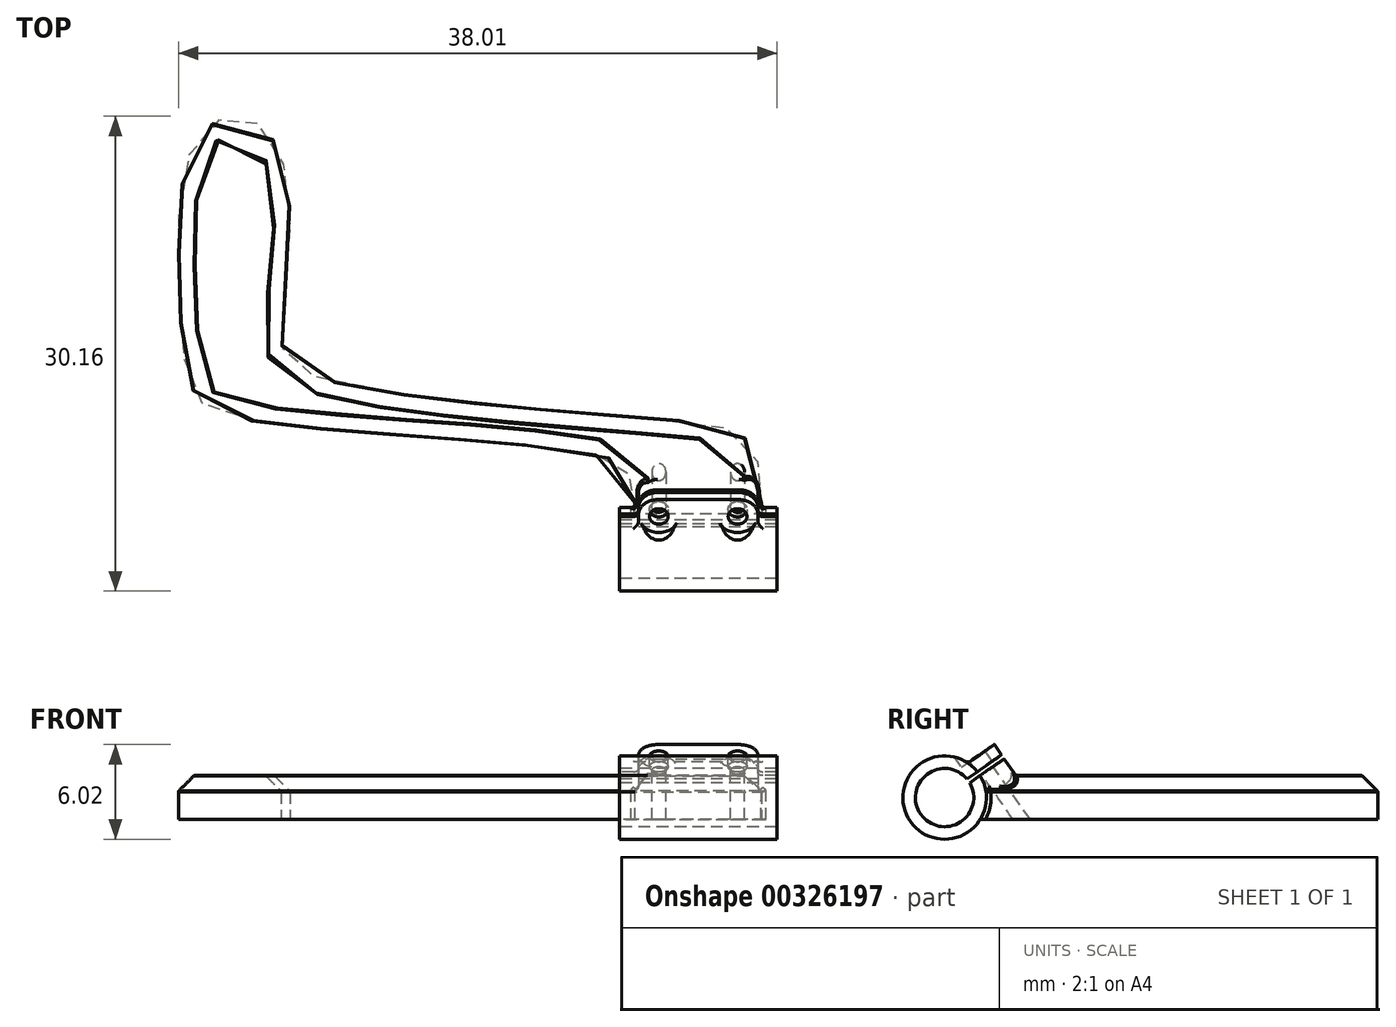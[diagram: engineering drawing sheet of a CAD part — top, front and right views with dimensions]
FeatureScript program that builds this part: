
annotation { "Feature Type Name" : "Feature", "Feature Type Description" : "" }
export const myFeature = defineFeature(function(context is Context, id is Id, definition is map)
    precondition{}
    {
        {
            var Q0;
            Q0=qCreatedBy(makeId("Top.planeOp"),FACE);
            var sketch = newSketch(context, id + "F0", { "sketchPlane" : qUnion([Q0])});
            skLineSegment(sketch, "E0", {"start": v(0, 0) * mm, "end": v(8, 0) * mm});
            skLineSegment(sketch, "E1", {"start": v(8, 0) * mm, "end": v(8, 0.6) * mm});
            skLineSegment(sketch, "E2", {"start": v(8, 0.6) * mm, "end": v(0, 0.6) * mm});
            skLineSegment(sketch, "E3", {"start": v(0, 0.6) * mm, "end": v(0, 0) * mm});
            skFitSpline(sketch, "E4", {"points": [v(0, 0.6) * mm, v(-0.36, 2.8) * mm, v(-2.22, 4.02) * mm, v(-24.68, 6.3) * mm, v(-28.15, 8.37) * mm, v(-29, 16.04) * mm, v(-28.1, 23.61) * mm, v(-25.63, 25.6) * mm, v(-23.1, 24.28) * mm, v(-21.95, 17.87) * mm, v(-22.45, 11.26) * mm, v(-20.46, 9.12) * mm, v(1.88, 6.35) * mm, v(7.53, 4.39) * mm, v(8, 0.6) * mm], "startDerivative": vector(0, 68.07) * mm, "endDerivative": vector(0, -27.38) * mm});
            skPoint(sketch, "E5", {"position": v(8, 0.3) * mm});
            skSolve(sketch);
        }
        {
            var Q0;
            Q0=qSketchRegion(id+"F0",true);
            extrude(context, id + "F1", {"entities" : qUnion([Q0]), "depth" : 2.8 * mm});
        }
        {
            var Q0;
            Q0=makeQuery(id+"F1.opExtrude","CAP_EDGE",EDGE,{"disambiguationData":[OSD([sQuery(id+"F0.wireOp",EDGE,"E4")])],"isStart":false});
            chamfer(context, id + "F2", {"entities" : qUnion([Q0]), "chamferType" : ChamferType.TWO_OFFSETS, "width1" : 1 * mm, "oppositeDirection" : false, "width2" : 1 * mm, "tangentPropagation" : true});
        }
        {
            var Q0;
            Q0=qCreatedBy(makeId("Right.planeOp"),FACE);
            var sketch = newSketch(context, id + "F3", { "sketchPlane" : qUnion([Q0])});
            skCircle(sketch, "E6.converted", {"center": v(-1.9, 1.4) * mm, "radius": 2.65 * mm});
            skCircle(sketch, "E7.converted", {"center": v(-1.9, 1.4) * mm, "radius": 1.85 * mm});
            skLineSegment(sketch, "E8", {"start": v(-1.9, 1.4) * mm, "end": v(0, 1.4) * mm, "construction": true});
            skSolve(sketch);
        }
        {
            var Q0;
            Q0=makeQuery(id+"F3.imprint","IMPRINT",FACE,{"disambiguationData":[TD([[makeQuery(id+"F3.imprint","IMPRINT",EDGE,{"derivedFrom":sQuery(id+"F3.wireOp",EDGE,"E6.converted")}),1.0]])]});
            extrude(context, id + "F4", {"entities" : qUnion([Q0]), "operationType" : NewBodyOperationType.ADD, "depth" : 9 * mm, "hasSecondDirection" : true, "secondDirectionOppositeDirection" : true, "secondDirectionDepth" : 1 * mm});
        }
        {
            var Q0;
            Q0=makeQuery(id+"F4.opExtrude","CAP_FACE",FACE,{"disambiguationData":[OSD([sQuery(id+"F3.wireOp",EDGE,"E6.converted"),sQuery(id+"F3.wireOp",EDGE,"E7.converted")])],"isStart":true});
            cPlane(context, id + "F5", {"entities" : qUnion([Q0]), "cplaneType" : CPlaneType.OFFSET, "offset" : 5 * mm, "oppositeDirection" : true, "width" : 150 * mm, "height" : 150 * mm});
        }
        {
            var Q0;
            Q0=qCreatedBy(id+"F5.planeOp",FACE);
            var sketch = newSketch(context, id + "F6", { "sketchPlane" : qUnion([Q0])});
            skLineSegment(sketch, "E9", {"start": v(1.9, 1.4) * mm, "end": v(0.51, 2.37) * mm, "construction": true});
            skLineSegment(sketch, "E10.0", {"start": v(2.16, 1.4) * mm, "end": v(0.16, 2.8) * mm});
            skLineSegment(sketch, "E11.0", {"start": v(1.64, 1.4) * mm, "end": v(-0.36, 2.8) * mm});
            skLineSegment(sketch, "E12", {"start": v(-0.36, 2.8) * mm, "end": v(0.16, 2.8) * mm});
            skLineSegment(sketch, "E13", {"start": v(2.16, 1.4) * mm, "end": v(1.64, 1.4) * mm});
            skLineSegment(sketch, "E14", {"start": v(0.16, 2.8) * mm, "end": v(-1.71, 4.11) * mm});
            skLineSegment(sketch, "E15", {"start": v(-1.71, 4.11) * mm, "end": v(-1.25, 4.77) * mm});
            skLineSegment(sketch, "E16", {"start": v(-1.25, 4.77) * mm, "end": v(1.56, 2.8) * mm});
            skLineSegment(sketch, "E17", {"start": v(1.56, 2.8) * mm, "end": v(1.1, 2.14) * mm});
            skLineSegment(sketch, "E18", {"start": v(-0.36, 2.8) * mm, "end": v(-1.88, 3.87) * mm});
            skLineSegment(sketch, "E19", {"start": v(-1.88, 3.87) * mm, "end": v(-2.63, 2.8) * mm});
            skLineSegment(sketch, "E20", {"start": v(-2.63, 2.8) * mm, "end": v(-0.36, 2.8) * mm});
            skCircle(sketch, "E21.0", {"center": v(1.9, 1.4) * mm, "radius": 1.85 * mm, "construction": true});
            skPoint(sketch, "E22", {"position": v(0.55, 3.5) * mm});
            skLineSegment(sketch, "E23", {"start": v(-2.63, 2.8) * mm, "end": v(-2.63, 1.7) * mm});
            skLineSegment(sketch, "E24", {"start": v(-2.63, 1.7) * mm, "end": v(0.79, 1.7) * mm});
            skLineSegment(sketch, "E25", {"start": v(0.79, 1.7) * mm, "end": v(0.93, 1.9) * mm});
            skCircle(sketch, "E26", {"center": v(1.9, 1.4) * mm, "radius": 2.5 * mm, "construction": true});
            skLineSegment(sketch, "E27", {"start": v(-1.71, 4.11) * mm, "end": v(-1.88, 3.87) * mm});
            skCircle(sketch, "E28", {"center": v(1.9, 1.4) * mm, "radius": 1.85 * mm});
            skLineSegment(sketch, "E29", {"start": v(-2.63, 2.8) * mm, "end": v(-2.88, 2.44) * mm});
            skLineSegment(sketch, "E30", {"start": v(-2.88, 2.44) * mm, "end": v(-2.88, 1.7) * mm});
            skLineSegment(sketch, "E31", {"start": v(-2.88, 1.7) * mm, "end": v(-2.63, 1.7) * mm});
            skSolve(sketch);
        }
        {
            var Q0;
            {var subQ0=sQuery(id+"F6.wireOp",EDGE,"E14");Q0=makeQuery(id+"F6.imprint","IMPRINT",FACE,{"disambiguationData":[TD([[makeQuery(id+"F6.imprint","IMPRINT",EDGE,{"derivedFrom":subQ0}),-1.0]])]});}
            var Q1;
            Q1=makeQuery(id+"F6.imprint","IMPRINT",FACE,{"disambiguationData":[TD([[makeQuery(id+"F6.imprint","IMPRINT",EDGE,{"derivedFrom":sQuery(id+"F6.wireOp",EDGE,"E18")}),1.0]])]});
            var Q2;
            {var subQ0=sQuery(id+"F6.wireOp",EDGE,"E20");Q2=makeQuery(id+"F6.imprint","IMPRINT",FACE,{"disambiguationData":[TD([[makeQuery(id+"F6.imprint","IMPRINT",EDGE,{"derivedFrom":subQ0}),-1.0]])]});}
            var Q3;
            Q3=makeQuery(id+"F6.imprint","IMPRINT",FACE,{"disambiguationData":[TD([[makeQuery(id+"F6.imprint","IMPRINT",EDGE,{"derivedFrom":sQuery(id+"F6.wireOp",EDGE,"E23")}),-1.0]])]});
            extrude(context, id + "F7", {"entities" : qUnion([Q0, Q1, Q2, Q3]), "operationType" : NewBodyOperationType.ADD, "depth" : 3.8 * mm, "hasSecondDirection" : true, "secondDirectionOppositeDirection" : true, "secondDirectionDepth" : 3.8 * mm});
        }
        {
            var Q0;
            {var subQ0=sQuery(id+"F6.wireOp",EDGE,"E12");Q0=makeQuery(id+"F6.imprint","IMPRINT",FACE,{"disambiguationData":[TD([[makeQuery(id+"F6.imprint","IMPRINT",EDGE,{"derivedFrom":subQ0}),-1.0]])]});}
            var Q1;
            Q1=makeQuery(id+"F6.imprint","IMPRINT",FACE,{"disambiguationData":[TD([[makeQuery(id+"F6.imprint","IMPRINT",EDGE,{"derivedFrom":sQuery(id+"F6.wireOp",EDGE,"E12")}),1.0]])]});
            var Q2;
            {var subQ1=sQuery(id+"F6.wireOp",EDGE,"E18");Q2=makeQuery(id+"F6.imprint","IMPRINT",FACE,{"disambiguationData":[TD([[makeQuery(id+"F6.imprint","IMPRINT",EDGE,{"derivedFrom":subQ1}),-1.0]])]});}
            extrude(context, id + "F8", {"entities" : qUnion([Q0, Q1, Q2]), "operationType" : NewBodyOperationType.REMOVE, "endBound" : BoundingType.THROUGH_ALL, "oppositeDirection" : true, "depth" : 25 * mm, "hasSecondDirection" : true, "secondDirectionBound" : BoundingType.THROUGH_ALL, "secondDirectionOppositeDirection" : false, "secondDirectionDepth" : 25 * mm});
        }
        {
            var Q0;
            Q0=makeQuery(id+"F7.opExtrude","SWEPT_FACE",FACE,{"disambiguationData":[OSD([sQuery(id+"F6.wireOp",EDGE,"E16")])]});
            var sketch = newSketch(context, id + "F9", { "sketchPlane" : qUnion([Q0])});
            skCircle(sketch, "E32", {"center": v(1.5, 2.46) * mm, "radius": 0.6 * mm});
            skCircle(sketch, "E33", {"center": v(6.5, 2.46) * mm, "radius": 0.6 * mm});
            skCircle(sketch, "E34", {"center": v(6.5, 2.46) * mm, "radius": 0.44 * mm});
            skCircle(sketch, "E35", {"center": v(1.5, 2.46) * mm, "radius": 0.44 * mm});
            skCircle(sketch, "E36", {"center": v(1.5, 2.46) * mm, "radius": 1.25 * mm});
            skCircle(sketch, "E37", {"center": v(6.5, 2.46) * mm, "radius": 1.25 * mm});
            skSolve(sketch);
        }
        {
            var Q0;
            Q0=makeQuery(id+"F9.imprint","IMPRINT",FACE,{"disambiguationData":[TD([[makeQuery(id+"F9.imprint","IMPRINT",EDGE,{"derivedFrom":sQuery(id+"F9.wireOp",EDGE,"E35")}),1.0]])]});
            var Q1;
            Q1=makeQuery(id+"F9.imprint","IMPRINT",FACE,{"disambiguationData":[TD([[makeQuery(id+"F9.imprint","IMPRINT",EDGE,{"derivedFrom":sQuery(id+"F9.wireOp",EDGE,"E34")}),1.0]])]});
            extrude(context, id + "F10", {"entities" : qUnion([Q0, Q1]), "operationType" : NewBodyOperationType.REMOVE, "endBound" : BoundingType.THROUGH_ALL, "oppositeDirection" : true, "depth" : 25 * mm});
        }
        {
            var Q0;
            Q0=makeQuery(id+"F9.imprint","IMPRINT",FACE,{"disambiguationData":[TD([[makeQuery(id+"F9.imprint","IMPRINT",EDGE,{"derivedFrom":sQuery(id+"F9.wireOp",EDGE,"E35")}),-1.0]])]});
            var Q1;
            Q1=makeQuery(id+"F9.imprint","IMPRINT",FACE,{"disambiguationData":[TD([[makeQuery(id+"F9.imprint","IMPRINT",EDGE,{"derivedFrom":sQuery(id+"F9.wireOp",EDGE,"E34")}),-1.0]])]});
            var Q2;
            {var subQ0=sQuery(id+"F9.wireOp",EDGE,"E32");var subQ1=makeQuery(id+"F7.boolean.opBoolean","INTERSECT",EDGE,{"derivedFrom":[makeQuery(id+"F4.opExtrude","SWEPT_FACE",FACE,{"disambiguationData":[OSD([sQuery(id+"F3.wireOp",EDGE,"E6.converted")])]}),makeQuery(id+"F7.opExtrude","SWEPT_FACE",FACE,{"disambiguationData":[OSD([sQuery(id+"F6.wireOp",EDGE,"E16")])]})]});var subQ2=makeQuery(id+"F9.imprint","INTERSECT",VERTEX,{"disambiguationData":[OD(0.0)],"derivedFrom":[subQ1,subQ0]});Q2=makeQuery(id+"F9.imprint","IMPRINT",FACE,{"disambiguationData":[TD([[makeQuery(id+"F9.imprint","IMPRINT",EDGE,{"disambiguationData":[TD([[subQ2,-1.0]])],"derivedFrom":subQ0}),1.0]])]});}
            var Q3;
            {var subQ0=sQuery(id+"F9.wireOp",EDGE,"E33");var subQ1=makeQuery(id+"F7.boolean.opBoolean","INTERSECT",EDGE,{"derivedFrom":[makeQuery(id+"F4.opExtrude","SWEPT_FACE",FACE,{"disambiguationData":[OSD([sQuery(id+"F3.wireOp",EDGE,"E6.converted")])]}),makeQuery(id+"F7.opExtrude","SWEPT_FACE",FACE,{"disambiguationData":[OSD([sQuery(id+"F6.wireOp",EDGE,"E16")])]})]});var subQ2=makeQuery(id+"F9.imprint","INTERSECT",VERTEX,{"disambiguationData":[OD(0.0)],"derivedFrom":[subQ1,subQ0]});Q3=makeQuery(id+"F9.imprint","IMPRINT",FACE,{"disambiguationData":[TD([[makeQuery(id+"F9.imprint","IMPRINT",EDGE,{"disambiguationData":[TD([[subQ2,1.0]])],"derivedFrom":subQ0}),1.0]])]});}
            extrude(context, id + "F11", {"entities" : qUnion([Q0, Q1, Q2, Q3]), "operationType" : NewBodyOperationType.REMOVE, "endBound" : BoundingType.UP_TO_NEXT, "oppositeDirection" : true, "depth" : 25 * mm, "hasSecondDirection" : true, "secondDirectionOppositeDirection" : false, "secondDirectionDepth" : 25 * mm});
        }
        {
            var Q0;
            {var subQ0=sQuery(id+"F9.wireOp",EDGE,"E36");var subQ1=makeQuery(id+"F7.boolean.opBoolean","INTERSECT",EDGE,{"derivedFrom":[makeQuery(id+"F4.opExtrude","SWEPT_FACE",FACE,{"disambiguationData":[OSD([sQuery(id+"F3.wireOp",EDGE,"E6.converted")])]}),makeQuery(id+"F7.opExtrude","SWEPT_FACE",FACE,{"disambiguationData":[OSD([sQuery(id+"F6.wireOp",EDGE,"E16")])]})]});var subQ2=makeQuery(id+"F9.imprint","INTERSECT",VERTEX,{"disambiguationData":[OD(0.0)],"derivedFrom":[subQ1,subQ0]});Q0=makeQuery(id+"F9.imprint","IMPRINT",FACE,{"disambiguationData":[TD([[makeQuery(id+"F9.imprint","IMPRINT",EDGE,{"disambiguationData":[TD([[subQ2,-1.0]])],"derivedFrom":subQ0}),1.0]])]});}
            var Q1;
            {var subQ0=sQuery(id+"F9.wireOp",EDGE,"E37");var subQ1=makeQuery(id+"F7.boolean.opBoolean","INTERSECT",EDGE,{"derivedFrom":[makeQuery(id+"F4.opExtrude","SWEPT_FACE",FACE,{"disambiguationData":[OSD([sQuery(id+"F3.wireOp",EDGE,"E6.converted")])]}),makeQuery(id+"F7.opExtrude","SWEPT_FACE",FACE,{"disambiguationData":[OSD([sQuery(id+"F6.wireOp",EDGE,"E16")])]})]});var subQ2=makeQuery(id+"F9.imprint","INTERSECT",VERTEX,{"disambiguationData":[OD(0.0)],"derivedFrom":[subQ1,subQ0]});Q1=makeQuery(id+"F9.imprint","IMPRINT",FACE,{"disambiguationData":[TD([[makeQuery(id+"F9.imprint","IMPRINT",EDGE,{"disambiguationData":[TD([[subQ2,1.0]])],"derivedFrom":subQ0}),1.0]])]});}
            extrude(context, id + "F12", {"entities" : qUnion([Q0, Q1]), "operationType" : NewBodyOperationType.REMOVE, "endBound" : BoundingType.UP_TO_NEXT, "depth" : 25 * mm});
        }
        {
            var Q0;
            Q0=makeQuery(id+"F7.opExtrude","CAP_EDGE",EDGE,{"disambiguationData":[OSD([sQuery(id+"F6.wireOp",EDGE,"E19")])],"isStart":false});
            var Q1;
            Q1=makeQuery(id+"F7.opExtrude","CAP_EDGE",EDGE,{"disambiguationData":[OSD([sQuery(id+"F6.wireOp",EDGE,"E15")])],"isStart":false});
            var Q2;
            Q2=makeQuery(id+"F7.opExtrude","CAP_EDGE",EDGE,{"disambiguationData":[OSD([sQuery(id+"F6.wireOp",EDGE,"E19")])],"isStart":true});
            var Q3;
            Q3=makeQuery(id+"F7.opExtrude","CAP_EDGE",EDGE,{"disambiguationData":[OSD([sQuery(id+"F6.wireOp",EDGE,"E15")])],"isStart":true});
            fillet(context, id + "F13", {"entities" : qUnion([Q0, Q1, Q2, Q3]), "radius" : 1.2 * mm, "tangentPropagation" : true, "allowEdgeOverflow" : false});
        }
        {
            var Q0;
            Q0=makeQuery(id+"F7.boolean.opBoolean","INTERSECT",EDGE,{"derivedFrom":[makeQuery(id+"F2.opChamfer","BLEND_FACE",FACE,{"disambiguationData":[OSD([sQuery(id+"F0.wireOp",EDGE,"E4")])]}),makeQuery(id+"F7.opExtrude","CAP_FACE",FACE,{"disambiguationData":[OSD([sQuery(id+"F6.wireOp",EDGE,"E11.0"),sQuery(id+"F6.wireOp",EDGE,"E18"),sQuery(id+"F6.wireOp",EDGE,"E19"),sQuery(id+"F6.wireOp",EDGE,"E23"),sQuery(id+"F6.wireOp",EDGE,"E24"),sQuery(id+"F6.wireOp",EDGE,"E28")])],"isStart":true})]});
            var Q1;
            Q1=makeQuery(id+"F13.opFillet","BLEND_EDGE",EDGE,{"blendedFrom":[makeQuery(id+"F7.opExtrude","CAP_EDGE",EDGE,{"disambiguationData":[OSD([sQuery(id+"F6.wireOp",EDGE,"E19")])],"isStart":false}),makeQuery(id+"F2.opChamfer","BLEND_FACE",FACE,{"disambiguationData":[OSD([sQuery(id+"F0.wireOp",EDGE,"E4")])]})],"blendedInto":[makeQuery(id+"F2.opChamfer","BLEND_FACE",FACE,{"disambiguationData":[OSD([sQuery(id+"F0.wireOp",EDGE,"E4")])]})]});
            var Q2;
            {var subQ0=sQuery(id+"F9.wireOp",EDGE,"E36");var subQ1=sQuery(id+"F6.wireOp",EDGE,"E16");var subQ2=sQuery(id+"F3.wireOp",EDGE,"E6.converted");var subQ3=makeQuery(id+"F7.opExtrude","SWEPT_FACE",FACE,{"disambiguationData":[OSD([subQ1])]});var subQ4=makeQuery(id+"F4.opExtrude","SWEPT_FACE",FACE,{"disambiguationData":[OSD([subQ2])]});var subQ5=sQuery(id+"F9.wireOp",EDGE,"E37");Q2=makeQuery(id+"F12.boolean.opBoolean","SPLIT",EDGE,{"disambiguationData":[TD([subQ4,subQ3,makeQuery(id+"F12.opExtrude","SWEPT_FACE",FACE,{"disambiguationData":[OSD([subQ0])]}),makeQuery(id+"F12.opExtrude","CAP_FACE",FACE,{"disambiguationData":[OSD([subQ2,subQ1,subQ0])],"isStart":true}),makeQuery(id+"F12.opExtrude","SWEPT_FACE",FACE,{"disambiguationData":[OSD([subQ5])]}),makeQuery(id+"F12.opExtrude","CAP_FACE",FACE,{"disambiguationData":[OSD([subQ2,subQ1,subQ5])],"isStart":true})])],"derivedFrom":makeQuery(id+"F7.boolean.opBoolean","INTERSECT",EDGE,{"derivedFrom":[subQ4,subQ3]})});}
            var Q3;
            {var subQ0=sQuery(id+"F6.wireOp",EDGE,"E16");var subQ1=makeQuery(id+"F7.opExtrude","SWEPT_FACE",FACE,{"disambiguationData":[OSD([subQ0])]});var subQ2=sQuery(id+"F9.wireOp",EDGE,"E36");var subQ3=sQuery(id+"F3.wireOp",EDGE,"E6.converted");var subQ4=makeQuery(id+"F4.opExtrude","SWEPT_FACE",FACE,{"disambiguationData":[OSD([subQ3])]});Q3=makeQuery(id+"F12.boolean.opBoolean","SPLIT",EDGE,{"disambiguationData":[TD([subQ4,makeQuery(id+"F7.opExtrude","CAP_FACE",FACE,{"disambiguationData":[OSD([sQuery(id+"F6.wireOp",EDGE,"E14"),sQuery(id+"F6.wireOp",EDGE,"E15"),subQ0,sQuery(id+"F6.wireOp",EDGE,"E28")])],"isStart":false}),subQ1,makeQuery(id+"F12.opExtrude","SWEPT_FACE",FACE,{"disambiguationData":[OSD([subQ2])]}),makeQuery(id+"F12.opExtrude","CAP_FACE",FACE,{"disambiguationData":[OSD([subQ3,subQ0,subQ2])],"isStart":true}),makeQuery(id+"F12.opExtrude","CAP_FACE",FACE,{"disambiguationData":[OSD([subQ3,subQ0,sQuery(id+"F9.wireOp",EDGE,"E37")])],"isStart":true})])],"derivedFrom":makeQuery(id+"F7.boolean.opBoolean","INTERSECT",EDGE,{"derivedFrom":[subQ4,subQ1]})});}
            var Q4;
            Q4=makeQuery(id+"F13.opFillet","BLEND_EDGE",EDGE,{"disambiguationData":[OD(1.0)],"blendedFrom":[makeQuery(id+"F7.opExtrude","CAP_EDGE",EDGE,{"disambiguationData":[OSD([sQuery(id+"F6.wireOp",EDGE,"E19")])],"isStart":true}),makeQuery(id+"F2.opChamfer","BLEND_FACE",FACE,{"disambiguationData":[OSD([sQuery(id+"F0.wireOp",EDGE,"E4")])]})],"blendedInto":[makeQuery(id+"F2.opChamfer","BLEND_FACE",FACE,{"disambiguationData":[OSD([sQuery(id+"F0.wireOp",EDGE,"E4")])]})]});
            var Q5;
            {var subQ0=sQuery(id+"F6.wireOp",EDGE,"E16");var subQ1=sQuery(id+"F3.wireOp",EDGE,"E6.converted");var subQ2=makeQuery(id+"F7.opExtrude","SWEPT_FACE",FACE,{"disambiguationData":[OSD([subQ0])]});var subQ3=makeQuery(id+"F4.opExtrude","SWEPT_FACE",FACE,{"disambiguationData":[OSD([subQ1])]});var subQ4=sQuery(id+"F9.wireOp",EDGE,"E37");Q5=makeQuery(id+"F12.boolean.opBoolean","SPLIT",EDGE,{"disambiguationData":[TD([subQ3,makeQuery(id+"F7.opExtrude","CAP_FACE",FACE,{"disambiguationData":[OSD([sQuery(id+"F6.wireOp",EDGE,"E14"),sQuery(id+"F6.wireOp",EDGE,"E15"),subQ0,sQuery(id+"F6.wireOp",EDGE,"E28")])],"isStart":true}),subQ2,makeQuery(id+"F12.opExtrude","CAP_FACE",FACE,{"disambiguationData":[OSD([subQ1,subQ0,sQuery(id+"F9.wireOp",EDGE,"E36")])],"isStart":true}),makeQuery(id+"F12.opExtrude","SWEPT_FACE",FACE,{"disambiguationData":[OSD([subQ4])]}),makeQuery(id+"F12.opExtrude","CAP_FACE",FACE,{"disambiguationData":[OSD([subQ1,subQ0,subQ4])],"isStart":true})])],"derivedFrom":makeQuery(id+"F7.boolean.opBoolean","INTERSECT",EDGE,{"derivedFrom":[subQ3,subQ2]})});}
            var Q6;
            Q6=makeQuery(id+"F4.boolean.opBoolean","INTERSECT",EDGE,{"derivedFrom":[makeQuery(id+"F1.opExtrude","SWEPT_FACE",FACE,{"disambiguationData":[OSD([sQuery(id+"F0.wireOp",EDGE,"E3")])]}),makeQuery(id+"F4.opExtrude","SWEPT_FACE",FACE,{"disambiguationData":[OSD([sQuery(id+"F3.wireOp",EDGE,"E6.converted")])]})]});
            var Q7;
            Q7=makeQuery(id+"F4.boolean.opBoolean","INTERSECT",EDGE,{"derivedFrom":[makeQuery(id+"F1.opExtrude","SWEPT_FACE",FACE,{"disambiguationData":[OSD([sQuery(id+"F0.wireOp",EDGE,"E1")])]}),makeQuery(id+"F4.opExtrude","SWEPT_FACE",FACE,{"disambiguationData":[OSD([sQuery(id+"F3.wireOp",EDGE,"E6.converted")])]})]});
            var Q8;
            Q8=makeQuery(id+"F4.boolean.opBoolean","INTERSECT",EDGE,{"disambiguationData":[OD(0.0)],"derivedFrom":[makeQuery(id+"F1.opExtrude","SWEPT_FACE",FACE,{"disambiguationData":[OSD([sQuery(id+"F0.wireOp",EDGE,"E4")])]}),makeQuery(id+"F4.opExtrude","SWEPT_FACE",FACE,{"disambiguationData":[OSD([sQuery(id+"F3.wireOp",EDGE,"E6.converted")])]})]});
            var Q9;
            Q9=makeQuery(id+"F7.boolean.opBoolean","INTERSECT",EDGE,{"derivedFrom":[makeQuery(id+"F1.opExtrude","CAP_FACE",FACE,{"disambiguationData":[OSD([sQuery(id+"F0.wireOp",EDGE,"E0"),sQuery(id+"F0.wireOp",EDGE,"E1"),sQuery(id+"F0.wireOp",EDGE,"E3"),sQuery(id+"F0.wireOp",EDGE,"E4")])],"isStart":false}),makeQuery(id+"F7.opExtrude","SWEPT_FACE",FACE,{"disambiguationData":[OSD([sQuery(id+"F6.wireOp",EDGE,"E19"),sQuery(id+"F6.wireOp",EDGE,"E29")])]})]});
            fillet(context, id + "F14", {"entities" : qUnion([Q0, Q1, Q2, Q3, Q4, Q5, Q6, Q7, Q8, Q9]), "radius" : 0.3 * mm, "tangentPropagation" : true, "allowEdgeOverflow" : false});
        }
        {
            var Q0;
            Q0=makeQuery(id+"F7eM0luwQxw6Xwf_1.opExtrude","TWEAK_EDGE",EDGE,{"derivedFrom":[makeQuery(id+"F1.opExtrude","CAP_EDGE",EDGE,{"disambiguationData":[OSD([sQuery(id+"F0.wireOp",EDGE,"E0")])],"isStart":true}),makeQuery(id+"F4.opExtrude","SWEPT_FACE",FACE,{"disambiguationData":[OSD([sQuery(id+"F3.wireOp",EDGE,"E6.converted")])]})]});
            var Q1;
            Q1=makeQuery(id+"F7.boolean.opBoolean","INTERSECT",EDGE,{"derivedFrom":[makeQuery(id+"F4.opExtrude","SWEPT_FACE",FACE,{"disambiguationData":[OSD([sQuery(id+"F3.wireOp",EDGE,"E6.converted")])]}),makeQuery(id+"F7.opExtrude","CAP_FACE",FACE,{"disambiguationData":[OSD([sQuery(id+"F6.wireOp",EDGE,"E11.0"),sQuery(id+"F6.wireOp",EDGE,"E18"),sQuery(id+"F6.wireOp",EDGE,"E19"),sQuery(id+"F6.wireOp",EDGE,"E23"),sQuery(id+"F6.wireOp",EDGE,"E24"),sQuery(id+"F6.wireOp",EDGE,"E25")])],"isStart":true})]});
            var Q2;
            Q2=makeQuery(id+"F7.boolean.opBoolean","INTERSECT",EDGE,{"derivedFrom":[makeQuery(id+"F4.opExtrude","SWEPT_FACE",FACE,{"disambiguationData":[OSD([sQuery(id+"F3.wireOp",EDGE,"E6.converted")])]}),makeQuery(id+"F7.opExtrude","CAP_FACE",FACE,{"disambiguationData":[OSD([sQuery(id+"F6.wireOp",EDGE,"E10.0"),sQuery(id+"F6.wireOp",EDGE,"E14"),sQuery(id+"F6.wireOp",EDGE,"E15"),sQuery(id+"F6.wireOp",EDGE,"E16"),sQuery(id+"F6.wireOp",EDGE,"E17")])],"isStart":true})]});
            var Q3;
            Q3=makeQuery(id+"F7.boolean.opBoolean","INTERSECT",EDGE,{"derivedFrom":[makeQuery(id+"F4.opExtrude","SWEPT_FACE",FACE,{"disambiguationData":[OSD([sQuery(id+"F3.wireOp",EDGE,"E6.converted")])]}),makeQuery(id+"F7.opExtrude","CAP_FACE",FACE,{"disambiguationData":[OSD([sQuery(id+"F6.wireOp",EDGE,"E11.0"),sQuery(id+"F6.wireOp",EDGE,"E18"),sQuery(id+"F6.wireOp",EDGE,"E19"),sQuery(id+"F6.wireOp",EDGE,"E23"),sQuery(id+"F6.wireOp",EDGE,"E24"),sQuery(id+"F6.wireOp",EDGE,"E25")])],"isStart":false})]});
            var Q4;
            Q4=makeQuery(id+"F7.boolean.opBoolean","INTERSECT",EDGE,{"derivedFrom":[makeQuery(id+"F4.opExtrude","SWEPT_FACE",FACE,{"disambiguationData":[OSD([sQuery(id+"F3.wireOp",EDGE,"E6.converted")])]}),makeQuery(id+"F7.opExtrude","CAP_FACE",FACE,{"disambiguationData":[OSD([sQuery(id+"F6.wireOp",EDGE,"E10.0"),sQuery(id+"F6.wireOp",EDGE,"E14"),sQuery(id+"F6.wireOp",EDGE,"E15"),sQuery(id+"F6.wireOp",EDGE,"E16"),sQuery(id+"F6.wireOp",EDGE,"E17")])],"isStart":false})]});
            var Q5;
            {var subQ0=sQuery(id+"F0.wireOp",EDGE,"E3");var subQ1=sQuery(id+"F0.wireOp",EDGE,"E0");var subQ2=makeQuery(id+"F2.opChamfer","BLEND_FACE",FACE,{"disambiguationData":[OSD([subQ0])]});var subQ3=makeQuery(id+"F4.opExtrude","SWEPT_FACE",FACE,{"disambiguationData":[OSD([sQuery(id+"F3.wireOp",EDGE,"E6.converted")])]});var subQ4=makeQuery(id+"F2.opChamfer","BLEND_EDGE",EDGE,{"blendedFrom":[makeQuery(id+"F1.opExtrude","CAP_EDGE",EDGE,{"disambiguationData":[OSD([subQ0])],"isStart":false}),makeQuery(id+"F1.opExtrude","SWEPT_FACE",FACE,{"disambiguationData":[OSD([subQ1])]})],"blendedInto":[makeQuery(id+"F1.opExtrude","SWEPT_FACE",FACE,{"disambiguationData":[OSD([subQ1])]})]});Q5=makeQuery(id+"F7.boolean.opBoolean","SPLIT",EDGE,{"disambiguationData":[TD([makeQuery(id+"F1.opExtrude","SWEPT_FACE",FACE,{"disambiguationData":[OSD([subQ0])]})])],"derivedFrom":makeQuery(id+"F7eM0luwQxw6Xwf_1.boolean.opBoolean","MERGE",EDGE,{"derivedFrom":[makeQuery(id+"F4.boolean.opBoolean","INTERSECT",EDGE,{"derivedFrom":[subQ2,subQ3]}),makeQuery(id+"F7eM0luwQxw6Xwf_1.opExtrude","TWEAK_EDGE",EDGE,{"derivedFrom":[subQ4,subQ3]})]})});}
            fillet(context, id + "F15", {"entities" : qUnion([Q0, Q1, Q2, Q3, Q4, Q5]), "radius" : 0.3 * mm, "tangentPropagation" : true, "allowEdgeOverflow" : false});
        }
        {
            var Q0;
            {var subQ0=sQuery(id+"F0.wireOp",EDGE,"E4");Q0=makeQuery(id+"F2.opChamfer","BLEND_EDGE",EDGE,{"blendedFrom":[makeQuery(id+"F1.opExtrude","CAP_EDGE",EDGE,{"disambiguationData":[OSD([subQ0])],"isStart":false}),makeQuery(id+"F1.opExtrude","SWEPT_FACE",FACE,{"disambiguationData":[OSD([subQ0])]})],"blendedInto":[makeQuery(id+"F1.opExtrude","SWEPT_FACE",FACE,{"disambiguationData":[OSD([subQ0])]})]});}
            var Q1;
            {var subQ0=sQuery(id+"F0.wireOp",EDGE,"E4");Q1=makeQuery(id+"F2.opChamfer","BLEND_EDGE",EDGE,{"blendedFrom":[makeQuery(id+"F1.opExtrude","CAP_EDGE",EDGE,{"disambiguationData":[OSD([subQ0])],"isStart":false}),makeQuery(id+"F1.opExtrude","CAP_FACE",FACE,{"disambiguationData":[OSD([sQuery(id+"F0.wireOp",EDGE,"E0"),sQuery(id+"F0.wireOp",EDGE,"E1"),sQuery(id+"F0.wireOp",EDGE,"E3"),subQ0])],"isStart":false})],"blendedInto":[makeQuery(id+"F1.opExtrude","CAP_FACE",FACE,{"disambiguationData":[OSD([sQuery(id+"F0.wireOp",EDGE,"E0"),sQuery(id+"F0.wireOp",EDGE,"E1"),sQuery(id+"F0.wireOp",EDGE,"E3"),subQ0])],"isStart":false})]});}
            var Q2;
            {var subQ0=sQuery(id+"F3.wireOp",EDGE,"E6.converted");var subQ1=sQuery(id+"F0.wireOp",EDGE,"E3");var subQ2=sQuery(id+"F0.wireOp",EDGE,"E0");var subQ3=makeQuery(id+"F2.opChamfer","BLEND_FACE",FACE,{"disambiguationData":[OSD([subQ1])]});var subQ4=makeQuery(id+"F4.opExtrude","SWEPT_FACE",FACE,{"disambiguationData":[OSD([subQ0])]});var subQ5=makeQuery(id+"F2.opChamfer","BLEND_EDGE",EDGE,{"blendedFrom":[makeQuery(id+"F1.opExtrude","CAP_EDGE",EDGE,{"disambiguationData":[OSD([subQ1])],"isStart":false}),makeQuery(id+"F1.opExtrude","SWEPT_FACE",FACE,{"disambiguationData":[OSD([subQ2])]})],"blendedInto":[makeQuery(id+"F1.opExtrude","SWEPT_FACE",FACE,{"disambiguationData":[OSD([subQ2])]})]});Q2=makeQuery(id+"F15.opFillet","BLEND_EDGE",EDGE,{"blendedFrom":[makeQuery(id+"F7.boolean.opBoolean","SPLIT",EDGE,{"disambiguationData":[TD([makeQuery(id+"F1.opExtrude","SWEPT_FACE",FACE,{"disambiguationData":[OSD([subQ1])]})])],"derivedFrom":makeQuery(id+"F7eM0luwQxw6Xwf_1.boolean.opBoolean","MERGE",EDGE,{"derivedFrom":[makeQuery(id+"F4.boolean.opBoolean","INTERSECT",EDGE,{"derivedFrom":[subQ3,subQ4]}),makeQuery(id+"F7eM0luwQxw6Xwf_1.opExtrude","TWEAK_EDGE",EDGE,{"derivedFrom":[subQ5,subQ4]})]})}),makeQuery(id+"F14.opFillet","BLEND_FACE",FACE,{"disambiguationData":[OSD([subQ2,subQ1,subQ0])]})],"blendedInto":[makeQuery(id+"F14.opFillet","BLEND_FACE",FACE,{"disambiguationData":[OSD([subQ2,subQ1,subQ0])]})]});}
            fillet(context, id + "F16", {"entities" : qUnion([Q0, Q1, Q2]), "radius" : 0.1 * mm, "tangentPropagation" : true, "allowEdgeOverflow" : false});
        }
    });
